# Revit family: QF_MOFFAT WALDORF_PC8140G
name_source: partatom
category: Specialty Equipment
revit_build: Autodesk Revit Architecture 2012 (Build: 20110309_2315(x64)
units: mm (PartAtom-declared; Revit-internal decimal feet)

## types (1)
- QF_MOFFAT WALDORF_PC8140G
    Body Finish = QF_Finishes_Stainless Steel
    Cold Water Connection Height = 0"
    Cold Water Flow = 0 GPM
    Cold Water Maximum Pressure = 0.00 psi
    Cold Water Minimum Pressure = 0.00 psi
    Cold Water RI Height = 0"
    Cold Water Size = 1"
    Cold Water Temperature Recommended = -460 °F
    Description = PASTA COOKER GAS SINGLE PAN
    Gas Connection Height = 0"
    Gas Input = 44547.0 Btu/h
    Gas KW = 13
    Gas RI Height = 0"
    Gas Size = 1"
    Height = 44 1/2"
    Indirect Waste Size = 1"
    Manufacturer = MOFFAT WALDORF
    Model = PC8140G
    URL = www.moffat.com
    URL Cutsheet = www.moffat.com
    Weight in Pounds = 180.7788

## geometry (parser evidence)
native form markers: Blend x10, Sweep x5
no freeform markers — native parametric forms only
